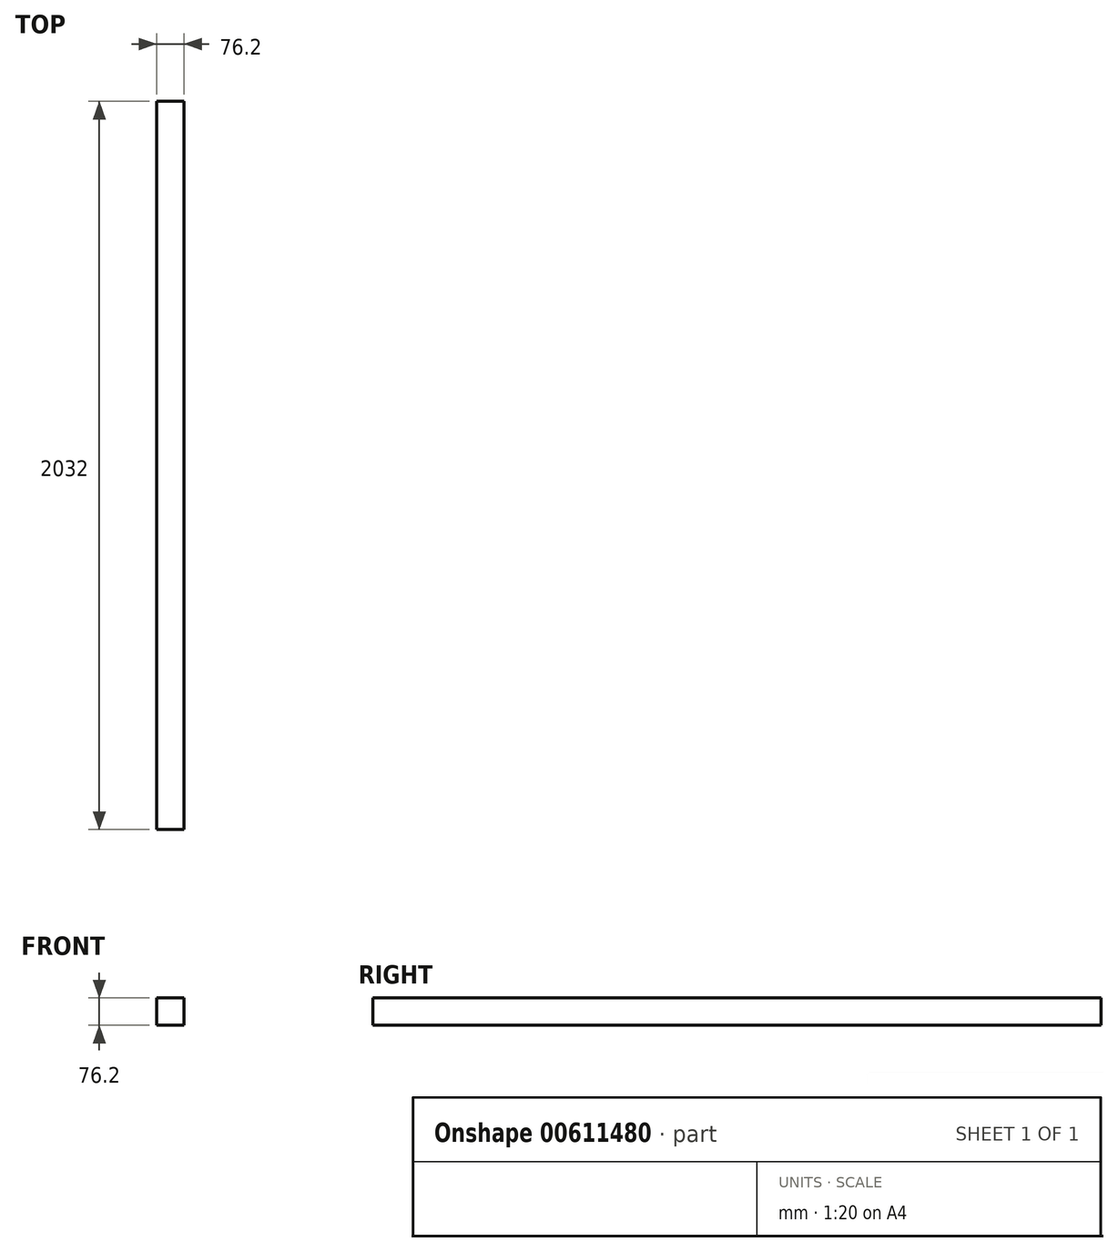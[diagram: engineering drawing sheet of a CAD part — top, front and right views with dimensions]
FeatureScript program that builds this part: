
annotation { "Feature Type Name" : "Feature", "Feature Type Description" : "" }
export const myFeature = defineFeature(function(context is Context, id is Id, definition is map)
    precondition{}
    {
        {
            var Q0;
            Q0=qCreatedBy(makeId("Front.planeOp"),FACE);
            var sketch = newSketch(context, id + "F0", { "sketchPlane" : qUnion([Q0])});
            skLineSegment(sketch, "E0.bottom", {"start": v(0, 0) * mm, "end": v(76.2, 0) * mm});
            skLineSegment(sketch, "E0.top", {"start": v(0, -76.2) * mm, "end": v(76.2, -76.2) * mm});
            skLineSegment(sketch, "E0.left", {"start": v(0, 0) * mm, "end": v(0, -76.2) * mm});
            skLineSegment(sketch, "E0.right", {"start": v(76.2, 0) * mm, "end": v(76.2, -76.2) * mm});
            skSolve(sketch);
        }
        {
            var Q0;
            Q0 = qSketchRegion(id + "F0", true);
            extrude(context, id + "F1", {"entities" : qUnion([Q0]), "depth" : 2032 * mm, "offsetDistance" : 25.4 * mm});
        }
    });
